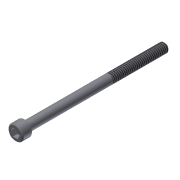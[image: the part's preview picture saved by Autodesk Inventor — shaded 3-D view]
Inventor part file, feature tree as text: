
AUTODESK INVENTOR PART (.ipt)
format: ipt  version: 2013 (Build 170138000, 138)  size: 100,352 bytes
history: native  units: in
note: dims shown in document units (in); Inventor stores cm internally (conversion verified against a paired STEP export)
features: extrude x3, sketch x3, chamfer x2, thread x1
ambient origin geometry x8: Origin, YZ Plane, XZ Plane, XY Plane, X Axis, Y Axis, Z Axis, Center Point
bodies: Solid1 (feature_tree)
feature tree (9):
  extrude  "Extrusion1"  Depth=0.164in TaperAngle=0.0deg
  extrude  "Extrusion2"  Depth=2.5in TaperAngle=0.0deg
  extrude  "Extrusion3"  Depth=0.08in TaperAngle=0.0deg
  thread  "Thread1"  [1 undecoded]
  chamfer  "Chamfer1"  Distance=0.02in Angle=45.0deg
  chamfer  "Chamfer2"  Distance=0.02in Angle=45.0deg
  sketch  "Sketch1"  dims[d0=0.27in d1=0.164in d2=0.0in]
  sketch  "Sketch2"  dims[d3=0.164in d4=2.5in d5=0.0in]
  sketch  "Sketch3"  dims[d6=0.1406in d7=0.08in d8=0.0in d9=1.0in d10=0.0in d11=0.02in d12=0.125in d13=45.0deg d14=0.02in d15=0.125in d16=45.0deg]
note: 1 required parameter value undecoded (feature->parameter linkage not recoverable at this tier; creation-order binding heuristic only, values carry confidence <= 0.55)
